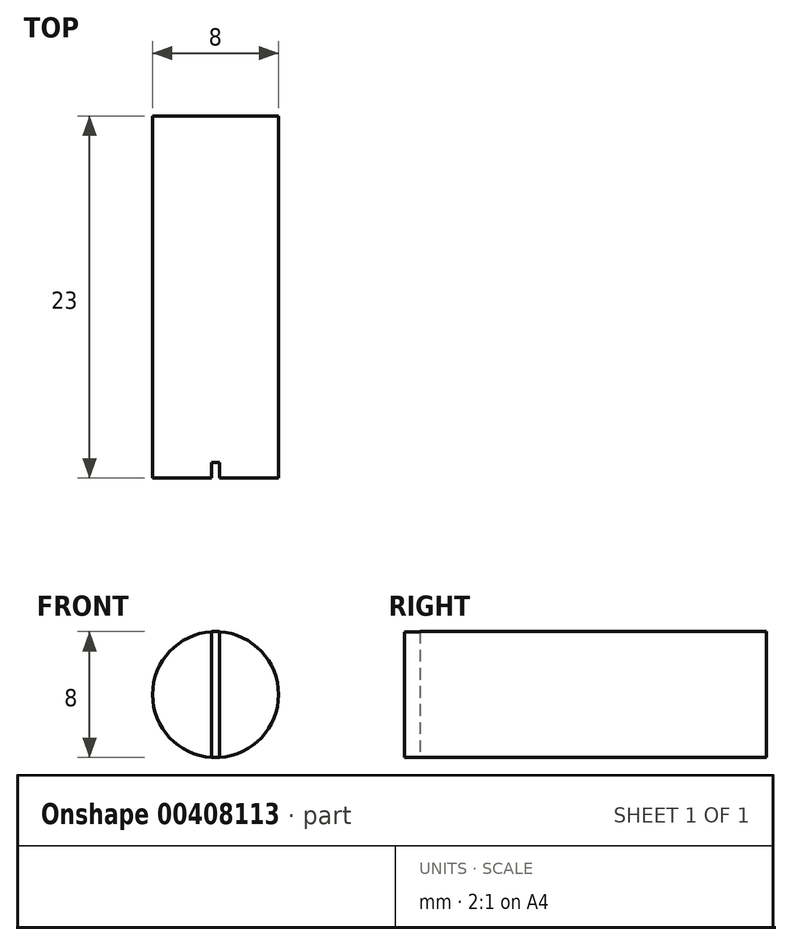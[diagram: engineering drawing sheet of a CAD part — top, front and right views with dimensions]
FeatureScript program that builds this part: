
annotation { "Feature Type Name" : "Feature", "Feature Type Description" : "" }
export const myFeature = defineFeature(function(context is Context, id is Id, definition is map)
    precondition{}
    {
        {
            var Q0;
            Q0=qCreatedBy(makeId("Front.planeOp"),FACE);
            var sketch = newSketch(context, id + "F0", { "sketchPlane" : qUnion([Q0])});
            skCircle(sketch, "E0", {"center": v(0, 0) * mm, "radius": 4 * mm});
            skSolve(sketch);
        }
        {
            var Q0;
            Q0 = qSketchRegion(id + "F0", true);
            extrude(context, id + "F1", {"entities" : qUnion([Q0]), "endBound" : BoundingType.SYMMETRIC, "depth" : 23 * mm});
        }
        {
            var Q0;
            Q0=makeQuery(id+"F1.opExtrude","CAP_FACE",FACE,{"disambiguationData":[OSD([sQuery(id+"F0.wireOp",EDGE,"E0")])],"isStart":false});
            var sketch = newSketch(context, id + "F2", { "sketchPlane" : qUnion([Q0])});
            skLineSegment(sketch, "E1.bottom", {"start": v(0.25, 5.65) * mm, "end": v(-0.25, 5.65) * mm});
            skLineSegment(sketch, "E1.top", {"start": v(0.25, -5.65) * mm, "end": v(-0.25, -5.65) * mm});
            skLineSegment(sketch, "E1.left", {"start": v(0.25, 5.65) * mm, "end": v(0.25, -5.65) * mm});
            skLineSegment(sketch, "E1.right", {"start": v(-0.25, 5.65) * mm, "end": v(-0.25, -5.65) * mm});
            skPoint(sketch, "E1.middle", {"position": v(0, 0) * mm});
            skSolve(sketch);
        }
        {
            var Q0;
            Q0 = qSketchRegion(id + "F2", true);
            extrude(context, id + "F3", {"entities" : qUnion([Q0]), "operationType" : NewBodyOperationType.REMOVE, "oppositeDirection" : true, "depth" : 1 * mm});
        }
    });
